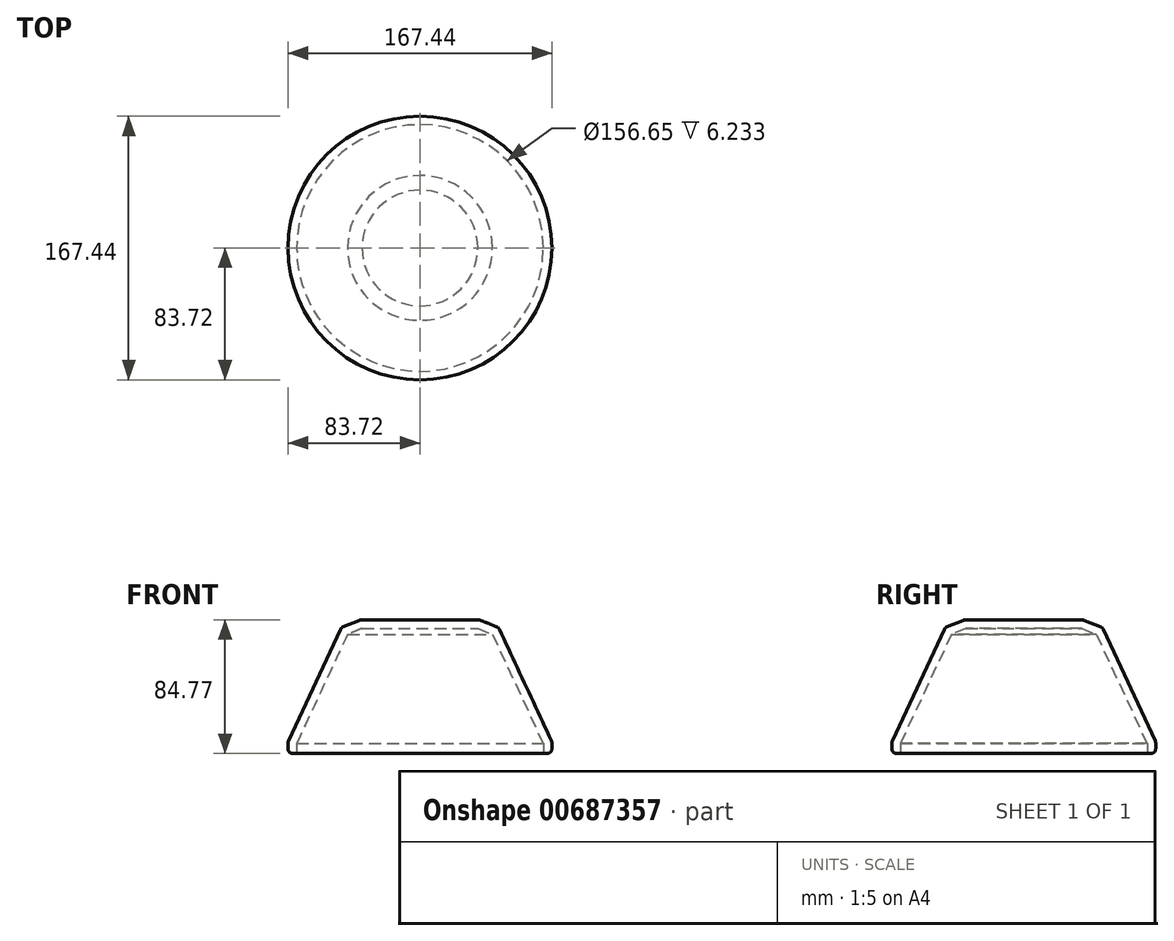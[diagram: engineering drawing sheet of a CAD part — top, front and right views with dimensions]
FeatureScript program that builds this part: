
annotation { "Feature Type Name" : "Feature", "Feature Type Description" : "" }
export const myFeature = defineFeature(function(context is Context, id is Id, definition is map)
    precondition{}
    {
        {
            var Q0;
            Q0=qCreatedBy(makeId("Front.planeOp"),FACE);
            var sketch = newSketch(context, id + "F0", { "sketchPlane" : qUnion([Q0])});
            skLineSegment(sketch, "E0", {"start": v(0, 66.2) * mm, "end": v(37.8, 66.2) * mm});
            skLineSegment(sketch, "E1", {"start": v(37.8, 66.2) * mm, "end": v(50, 61.25) * mm});
            skLineSegment(sketch, "E2", {"start": v(50, 61.25) * mm, "end": v(83.72, -11.14) * mm});
            skLineSegment(sketch, "E3", {"start": v(83.72, -11.14) * mm, "end": v(83.72, -18.57) * mm});
            skLineSegment(sketch, "E4", {"start": v(83.72, -18.57) * mm, "end": v(78.32, -18.57) * mm});
            skLineSegment(sketch, "E5", {"start": v(0, 60.8) * mm, "end": v(0, 66.2) * mm});
            skLineSegment(sketch, "E6.1", {"start": v(5.4, 60.8) * mm, "end": v(36.75, 60.8) * mm});
            skLineSegment(sketch, "E6.2", {"start": v(36.75, 60.8) * mm, "end": v(46, 57.04) * mm});
            skLineSegment(sketch, "E6.4", {"start": v(46, 57.04) * mm, "end": v(78.32, -12.34) * mm});
            skLineSegment(sketch, "E6.5", {"start": v(78.32, -12.34) * mm, "end": v(78.32, -13.17) * mm});
            skLineSegment(sketch, "E7", {"start": v(78.32, -12.34) * mm, "end": v(78.32, -18.57) * mm});
            skLineSegment(sketch, "E8", {"start": v(5.4, 60.8) * mm, "end": v(0, 60.8) * mm});
            skPoint(sketch, "E9.orphan", {"position": v(0, -18.57) * mm});
            skSolve(sketch);
        }
        {
            var Q0;
            Q0 = qSketchRegion(id + "F0", true);
            var Q1;
            Q1=sQuery(id+"F0.wireOp",EDGE,"E5");
            revolve(context, id + "F1", {"entities" : qUnion([Q0]), "axis" : qUnion([Q1]), "revolveType" : RevolveType.FULL});
        }
        {
            var Q0;
            Q0=makeQuery(id+"F1.opRevolve","SWEPT_FACE",FACE,{"disambiguationData":[OSD([sQuery(id+"F0.wireOp",EDGE,"E3")])]});
            var Q1;
            Q1=makeQuery(id+"F1.opRevolve","SWEPT_FACE",FACE,{"disambiguationData":[OSD([sQuery(id+"F0.wireOp",EDGE,"E1")])]});
            var Q2;
            Q2=makeQuery(id+"F1.opRevolve","SWEPT_EDGE",EDGE,{"disambiguationData":[OSD([sQuery(id+"F0.wireOp",EDGE,"E0"),sQuery(id+"F0.wireOp",EDGE,"E1")])]});
            var Q3;
            Q3=makeQuery(id+"F1.opRevolve","SWEPT_FACE",FACE,{"disambiguationData":[OSD([sQuery(id+"F0.wireOp",EDGE,"E2")])]});
            fillet(context, id + "F2", {"entities" : qUnion([Q0, Q1, Q2, Q3]), "radius" : 2.69 * mm, "tangentPropagation" : true, "allowEdgeOverflow" : false});
        }
    });
